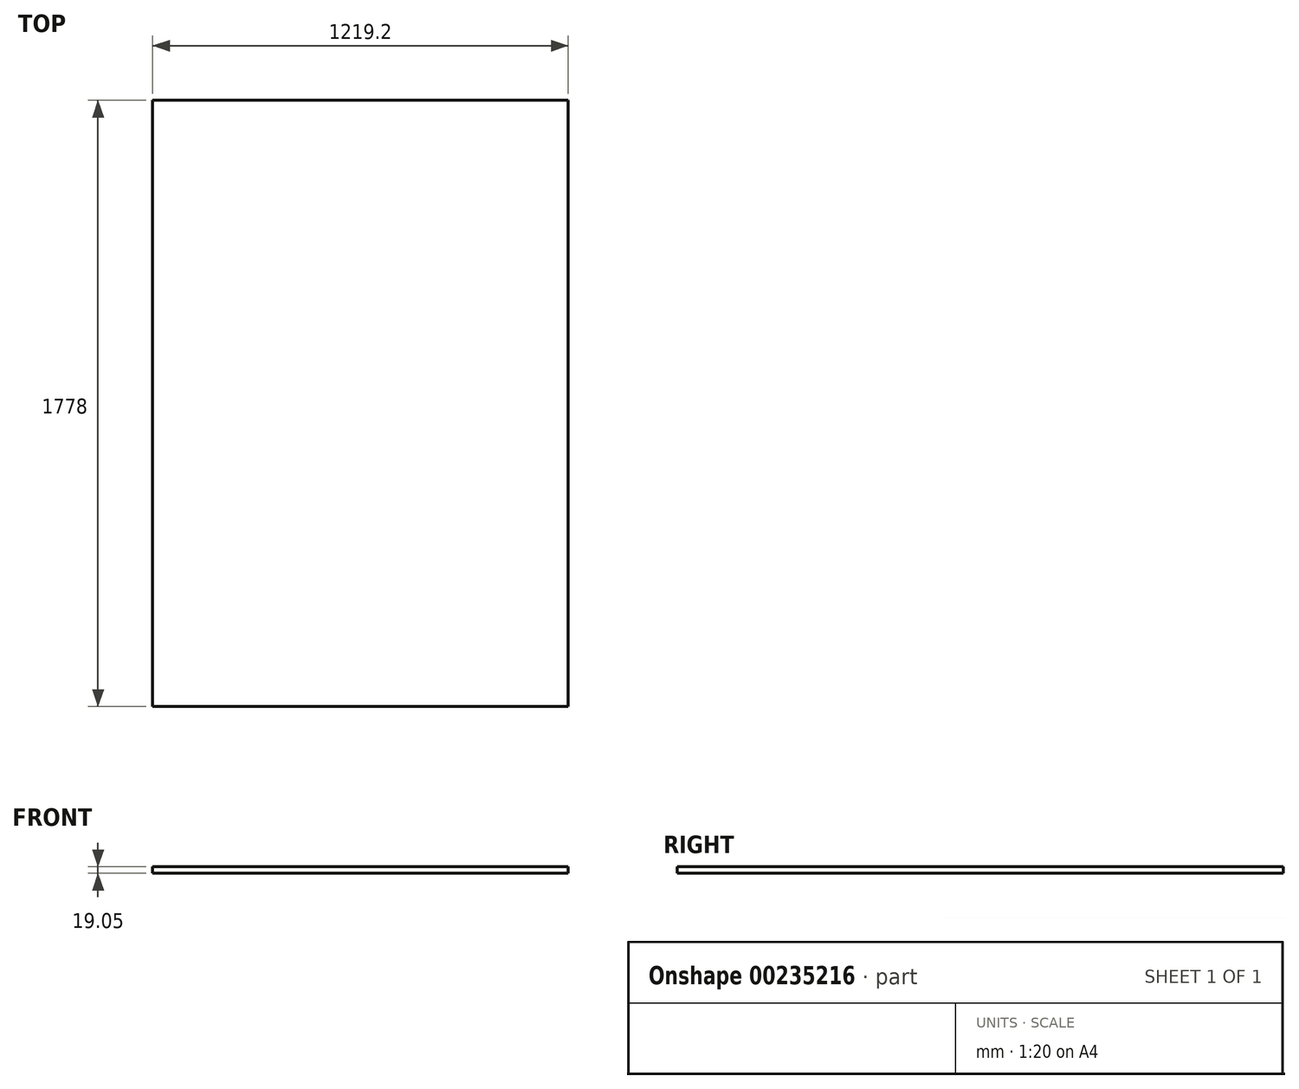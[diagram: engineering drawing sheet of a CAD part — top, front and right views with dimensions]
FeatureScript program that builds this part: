
annotation { "Feature Type Name" : "Feature", "Feature Type Description" : "" }
export const myFeature = defineFeature(function(context is Context, id is Id, definition is map)
    precondition{}
    {
        {
            var Q0;
            Q0=qCreatedBy(makeId("Top.planeOp"),FACE);
            var sketch = newSketch(context, id + "F0", { "sketchPlane" : qUnion([Q0])});
            skLineSegment(sketch, "E0.bottom", {"start": v(-609.6, 889) * mm, "end": v(609.6, 889) * mm});
            skLineSegment(sketch, "E0.top", {"start": v(-609.6, -889) * mm, "end": v(609.6, -889) * mm});
            skLineSegment(sketch, "E0.left", {"start": v(-609.6, 889) * mm, "end": v(-609.6, -889) * mm});
            skLineSegment(sketch, "E0.right", {"start": v(609.6, 889) * mm, "end": v(609.6, -889) * mm});
            skLineSegment(sketch, "E1", {"start": v(0, 889) * mm, "end": v(0, -889) * mm, "construction": true});
            skLineSegment(sketch, "E2", {"start": v(-609.6, 0) * mm, "end": v(609.6, 0) * mm, "construction": true});
            skSolve(sketch);
        }
        {
            var Q0;
            Q0=makeQuery(id+"F0.imprint","IMPRINT",FACE,{"disambiguationData":[TD([[makeQuery(id+"F0.imprint","IMPRINT",EDGE,{"derivedFrom":sQuery(id+"F0.wireOp",EDGE,"E0.bottom")}),-1.0]])]});
            extrude(context, id + "F1", {"entities" : qUnion([Q0]), "depth" : 19.05 * mm});
        }
    });
